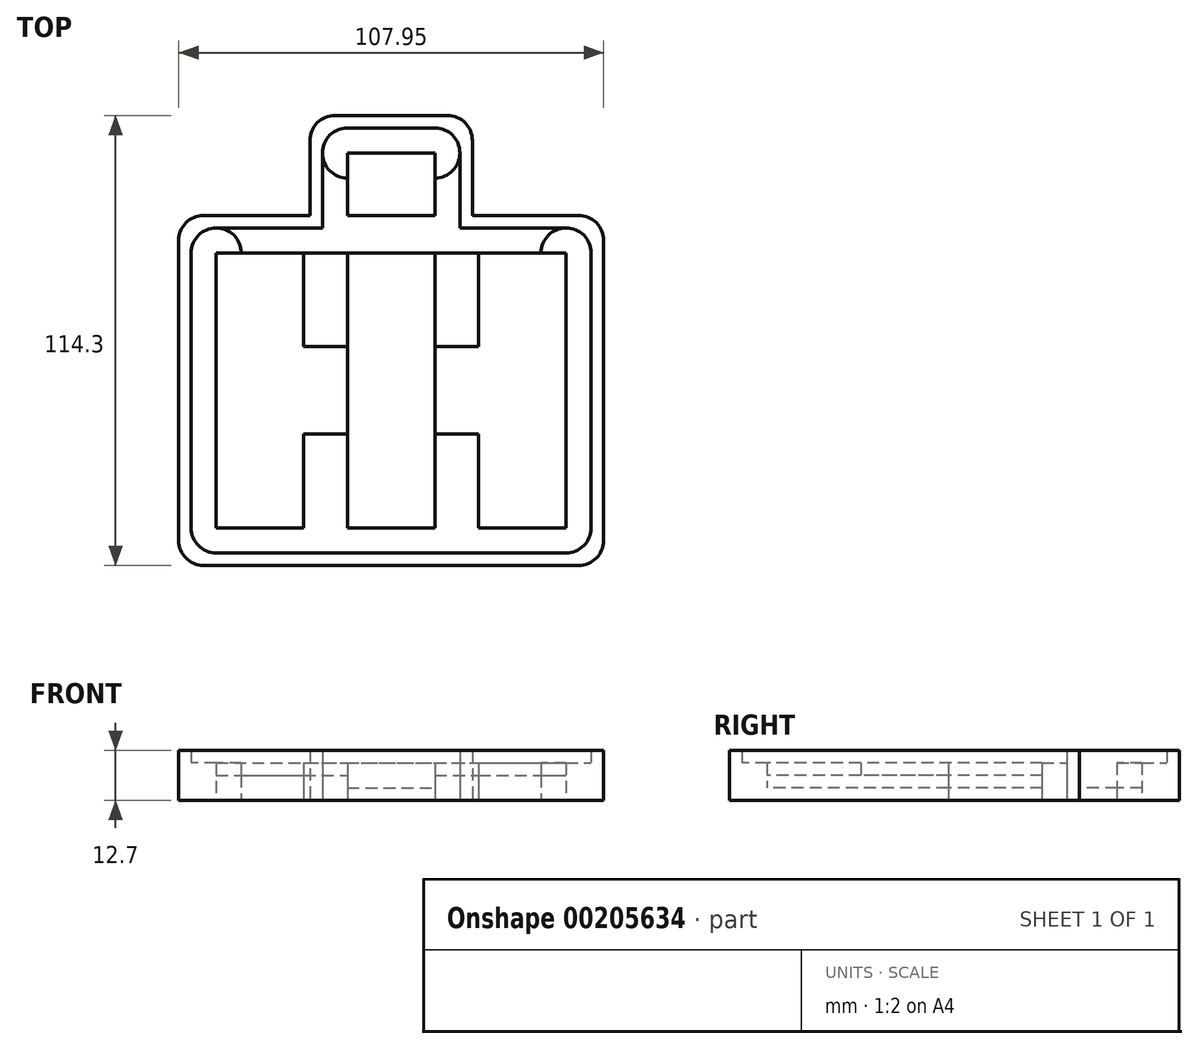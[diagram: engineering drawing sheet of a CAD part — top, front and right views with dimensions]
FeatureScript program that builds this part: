
annotation { "Feature Type Name" : "Feature", "Feature Type Description" : "" }
export const myFeature = defineFeature(function(context is Context, id is Id, definition is map)
    precondition{}
    {
        {
            var Q0;
            Q0=qCreatedBy(makeId("Top.planeOp"),FACE);
            var sketch = newSketch(context, id + "F0", { "sketchPlane" : qUnion([Q0])});
            skLineSegment(sketch, "E0.bottom", {"start": v(-34.36, 39.37) * mm, "end": v(-12.13, 39.37) * mm});
            skLineSegment(sketch, "E0.top", {"start": v(-34.36, -30.48) * mm, "end": v(-12.13, -30.48) * mm});
            skLineSegment(sketch, "E0.left", {"start": v(-34.36, 39.37) * mm, "end": v(-34.36, -30.48) * mm});
            skLineSegment(sketch, "E0.right", {"start": v(-12.13, 39.37) * mm, "end": v(-12.13, 15.56) * mm});
            skLineSegment(sketch, "E1.bottom", {"start": v(-12.13, 15.56) * mm, "end": v(32.32, 15.56) * mm});
            skLineSegment(sketch, "E1.top", {"start": v(-12.13, -6.67) * mm, "end": v(-1.02, -6.67) * mm});
            skLineSegment(sketch, "E1.left", {"start": v(-12.13, 15.56) * mm, "end": v(-12.13, -6.67) * mm});
            skLineSegment(sketch, "E1.right", {"start": v(32.32, 15.56) * mm, "end": v(32.32, 15.56) * mm});
            skLineSegment(sketch, "E2.bottom", {"start": v(32.32, 39.37) * mm, "end": v(54.54, 39.37) * mm});
            skLineSegment(sketch, "E2.top", {"start": v(32.32, -30.48) * mm, "end": v(54.54, -30.48) * mm});
            skLineSegment(sketch, "E2.left", {"start": v(32.32, 39.37) * mm, "end": v(32.32, 15.56) * mm});
            skLineSegment(sketch, "E2.right", {"start": v(54.54, 39.37) * mm, "end": v(54.54, -30.48) * mm});
            skLineSegment(sketch, "E3", {"start": v(-12.13, -6.67) * mm, "end": v(-12.13, -30.48) * mm});
            skLineSegment(sketch, "E4", {"start": v(32.32, 15.56) * mm, "end": v(32.32, -6.67) * mm});
            skLineSegment(sketch, "E5", {"start": v(32.32, -6.67) * mm, "end": v(32.32, -30.48) * mm});
            skLineSegment(sketch, "E6.bottom", {"start": v(-1.02, 39.37) * mm, "end": v(21.2, 39.37) * mm});
            skLineSegment(sketch, "E6.top", {"start": v(-1.02, -30.48) * mm, "end": v(21.2, -30.48) * mm});
            skLineSegment(sketch, "E6.left", {"start": v(-1.02, 39.37) * mm, "end": v(-1.02, -6.67) * mm});
            skLineSegment(sketch, "E6.right", {"start": v(21.2, 39.37) * mm, "end": v(21.2, 15.56) * mm});
            skLineSegment(sketch, "E7", {"start": v(21.2, 15.56) * mm, "end": v(21.2, -6.67) * mm});
            skLineSegment(sketch, "E8", {"start": v(21.2, -6.67) * mm, "end": v(21.2, -6.67) * mm});
            skLineSegment(sketch, "E9", {"start": v(-1.02, -6.67) * mm, "end": v(-1.02, -30.48) * mm});
            skLineSegment(sketch, "E10", {"start": v(21.2, -6.67) * mm, "end": v(21.2, -30.48) * mm});
            skLineSegment(sketch, "E11", {"start": v(21.2, -6.67) * mm, "end": v(32.32, -6.67) * mm});
            skLineSegment(sketch, "E12", {"start": v(-1.02, -6.67) * mm, "end": v(21.2, -6.67) * mm});
            skLineSegment(sketch, "E13.bottom", {"start": v(-1.02, 64.77) * mm, "end": v(21.2, 64.77) * mm});
            skLineSegment(sketch, "E13.top", {"start": v(-1.02, 45.72) * mm, "end": v(21.2, 45.72) * mm});
            skLineSegment(sketch, "E13.left", {"start": v(-1.02, 64.77) * mm, "end": v(-1.02, 45.72) * mm});
            skLineSegment(sketch, "E13.right", {"start": v(21.2, 64.77) * mm, "end": v(21.2, 45.72) * mm});
            skLineSegment(sketch, "E14.bottom", {"start": v(-34.36, 39.37) * mm, "end": v(54.54, 39.37) * mm});
            skLineSegment(sketch, "E14.top", {"start": v(-34.36, 45.72) * mm, "end": v(54.54, 45.72) * mm});
            skLineSegment(sketch, "E14.left", {"start": v(-34.36, 39.37) * mm, "end": v(-34.36, 45.72) * mm});
            skLineSegment(sketch, "E14.right", {"start": v(54.54, 39.37) * mm, "end": v(54.54, 45.72) * mm});
            skLineSegment(sketch, "E15.bottom", {"start": v(-34.36, -30.48) * mm, "end": v(54.54, -30.48) * mm});
            skLineSegment(sketch, "E15.top", {"start": v(-34.36, -36.83) * mm, "end": v(54.54, -36.83) * mm});
            skLineSegment(sketch, "E15.left", {"start": v(-34.36, -30.48) * mm, "end": v(-34.36, -36.83) * mm});
            skLineSegment(sketch, "E15.right", {"start": v(54.54, -30.48) * mm, "end": v(54.54, -36.83) * mm});
            skLineSegment(sketch, "E16.bottom", {"start": v(-34.36, 39.37) * mm, "end": v(-40.7, 39.37) * mm});
            skLineSegment(sketch, "E16.top", {"start": v(-34.36, -30.48) * mm, "end": v(-40.7, -30.48) * mm});
            skLineSegment(sketch, "E16.right", {"start": v(-40.7, 39.37) * mm, "end": v(-40.7, -30.48) * mm});
            skLineSegment(sketch, "E17.bottom", {"start": v(54.54, 39.37) * mm, "end": v(60.9, 39.37) * mm});
            skLineSegment(sketch, "E17.top", {"start": v(54.54, -30.48) * mm, "end": v(60.9, -30.48) * mm});
            skLineSegment(sketch, "E17.right", {"start": v(60.9, 39.37) * mm, "end": v(60.9, -30.48) * mm});
            skLineSegment(sketch, "E18.bottom", {"start": v(21.2, 64.77) * mm, "end": v(27.55, 64.77) * mm});
            skLineSegment(sketch, "E18.top", {"start": v(21.2, 45.72) * mm, "end": v(27.55, 45.72) * mm});
            skLineSegment(sketch, "E18.right", {"start": v(27.55, 64.77) * mm, "end": v(27.55, 45.72) * mm});
            skLineSegment(sketch, "E19.bottom", {"start": v(-1.02, 64.77) * mm, "end": v(-7.37, 64.77) * mm});
            skLineSegment(sketch, "E19.top", {"start": v(-1.02, 45.72) * mm, "end": v(-7.37, 45.72) * mm});
            skLineSegment(sketch, "E19.right", {"start": v(-7.37, 64.77) * mm, "end": v(-7.37, 45.72) * mm});
            skLineSegment(sketch, "E20.top", {"start": v(-1.02, 71.12) * mm, "end": v(21.2, 71.12) * mm});
            skLineSegment(sketch, "E20.left", {"start": v(-1.02, 64.77) * mm, "end": v(-1.02, 71.12) * mm});
            skLineSegment(sketch, "E20.right", {"start": v(21.2, 64.77) * mm, "end": v(21.2, 71.12) * mm});
            skCircle(sketch, "E21", {"center": v(-34.36, 39.37) * mm, "radius": 6.35 * mm});
            skCircle(sketch, "E22", {"center": v(54.54, 39.37) * mm, "radius": 6.35 * mm});
            skCircle(sketch, "E23", {"center": v(-34.36, -30.48) * mm, "radius": 6.35 * mm});
            skCircle(sketch, "E24", {"center": v(54.54, -30.48) * mm, "radius": 6.35 * mm});
            skCircle(sketch, "E25", {"center": v(21.2, 64.77) * mm, "radius": 6.35 * mm});
            skCircle(sketch, "E26", {"center": v(-1.02, 64.77) * mm, "radius": 6.35 * mm});
            skLineSegment(sketch, "E27.bottom", {"start": v(-43.88, 48.9) * mm, "end": v(64.07, 48.9) * mm});
            skLineSegment(sketch, "E27.top", {"start": v(-43.88, -40) * mm, "end": v(64.07, -40) * mm});
            skLineSegment(sketch, "E27.left", {"start": v(-43.88, 48.9) * mm, "end": v(-43.88, -40) * mm});
            skLineSegment(sketch, "E27.right", {"start": v(64.07, 48.9) * mm, "end": v(64.07, -40) * mm});
            skLineSegment(sketch, "E28.bottom", {"start": v(-10.55, 48.9) * mm, "end": v(30.73, 48.9) * mm});
            skLineSegment(sketch, "E28.top", {"start": v(-10.55, 74.3) * mm, "end": v(30.73, 74.3) * mm});
            skLineSegment(sketch, "E28.left", {"start": v(-10.55, 48.9) * mm, "end": v(-10.55, 74.3) * mm});
            skLineSegment(sketch, "E28.right", {"start": v(30.73, 48.9) * mm, "end": v(30.73, 74.3) * mm});
            skSolve(sketch);
        }
        {
            var Q0;
            {var subQ0=sQuery(id+"F0.wireOp",EDGE,"E6.right");Q0=makeQuery(id+"F0.imprint","IMPRINT",FACE,{"disambiguationData":[TD([[makeQuery(id+"F0.imprint","IMPRINT",EDGE,{"derivedFrom":subQ0}),-1.0]])]});}
            var Q1;
            {var subQ0=sQuery(id+"F0.wireOp",EDGE,"E7");Q1=makeQuery(id+"F0.imprint","IMPRINT",FACE,{"disambiguationData":[TD([[makeQuery(id+"F0.imprint","IMPRINT",EDGE,{"derivedFrom":subQ0}),-1.0]])]});}
            var Q2;
            {var subQ0=sQuery(id+"F0.wireOp",EDGE,"E9");Q2=makeQuery(id+"F0.imprint","IMPRINT",FACE,{"disambiguationData":[TD([[makeQuery(id+"F0.imprint","IMPRINT",EDGE,{"derivedFrom":subQ0}),1.0]])]});}
            var Q3;
            {var subQ0=sQuery(id+"F0.wireOp",EDGE,"E26");var subQ1=sQuery(id+"F0.wireOp",EDGE,"E13.bottom");var subQ2=makeQuery(id+"F0.imprint","INTERSECT",VERTEX,{"derivedFrom":[subQ1,subQ0]});Q3=makeQuery(id+"F0.imprint","IMPRINT",FACE,{"disambiguationData":[TD([[makeQuery(id+"F0.imprint","IMPRINT",EDGE,{"disambiguationData":[TD([[subQ2,-1.0]])],"derivedFrom":subQ1}),-1.0]])]});}
            var Q4;
            {var subQ1=sQuery(id+"F0.wireOp",EDGE,"E13.left");var subQ3=sQuery(id+"F0.wireOp",EDGE,"E26");var subQ4=makeQuery(id+"F0.imprint","INTERSECT",VERTEX,{"derivedFrom":[subQ1,subQ3]});Q4=makeQuery(id+"F0.imprint","IMPRINT",FACE,{"disambiguationData":[TD([[makeQuery(id+"F0.imprint","IMPRINT",EDGE,{"disambiguationData":[TD([[subQ4,-1.0]])],"derivedFrom":subQ3}),1.0]])]});}
            var Q5;
            {var subQ1=sQuery(id+"F0.wireOp",EDGE,"E13.right");var subQ3=sQuery(id+"F0.wireOp",EDGE,"E25");var subQ4=makeQuery(id+"F0.imprint","INTERSECT",VERTEX,{"derivedFrom":[subQ1,subQ3]});Q5=makeQuery(id+"F0.imprint","IMPRINT",FACE,{"disambiguationData":[TD([[makeQuery(id+"F0.imprint","IMPRINT",EDGE,{"disambiguationData":[TD([[subQ4,1.0]])],"derivedFrom":subQ3}),1.0]])]});}
            extrude(context, id + "F1", {"entities" : qUnion([Q0, Q1, Q2, Q3, Q4, Q5]), "depth" : 3.17 * mm});
        }
        {
            var Q0;
            {var subQ1=sQuery(id+"F0.wireOp",EDGE,"E2.left");Q0=makeQuery(id+"F0.imprint","IMPRINT",FACE,{"disambiguationData":[TD([[makeQuery(id+"F0.imprint","IMPRINT",EDGE,{"derivedFrom":subQ1}),1.0]])]});}
            var Q1;
            {var subQ1=sQuery(id+"F0.wireOp",EDGE,"E0.right");Q1=makeQuery(id+"F0.imprint","IMPRINT",FACE,{"disambiguationData":[TD([[makeQuery(id+"F0.imprint","IMPRINT",EDGE,{"derivedFrom":subQ1}),-1.0]])]});}
            var Q2;
            {var subQ4=sQuery(id+"F0.wireOp",EDGE,"E1.top");Q2=makeQuery(id+"F0.imprint","IMPRINT",FACE,{"disambiguationData":[TD([[makeQuery(id+"F0.imprint","IMPRINT",EDGE,{"derivedFrom":subQ4}),1.0]])]});}
            var Q3;
            {var subQ0=sQuery(id+"F0.wireOp",EDGE,"E4");Q3=makeQuery(id+"F0.imprint","IMPRINT",FACE,{"disambiguationData":[TD([[makeQuery(id+"F0.imprint","IMPRINT",EDGE,{"derivedFrom":subQ0}),-1.0]])]});}
            var Q4;
            {var subQ1=sQuery(id+"F0.wireOp",EDGE,"E14.bottom");var subQ3=sQuery(id+"F0.wireOp",EDGE,"E21");var subQ4=makeQuery(id+"F0.imprint","INTERSECT",VERTEX,{"derivedFrom":[subQ1,subQ3]});Q4=makeQuery(id+"F0.imprint","IMPRINT",FACE,{"disambiguationData":[TD([[makeQuery(id+"F0.imprint","IMPRINT",EDGE,{"disambiguationData":[TD([[subQ4,1.0]])],"derivedFrom":subQ3}),1.0]])]});}
            var Q5;
            {var subQ1=sQuery(id+"F0.wireOp",EDGE,"E15.bottom");var subQ3=sQuery(id+"F0.wireOp",EDGE,"E23");var subQ4=makeQuery(id+"F0.imprint","INTERSECT",VERTEX,{"derivedFrom":[subQ1,subQ3]});Q5=makeQuery(id+"F0.imprint","IMPRINT",FACE,{"disambiguationData":[TD([[makeQuery(id+"F0.imprint","IMPRINT",EDGE,{"disambiguationData":[TD([[subQ4,-1.0]])],"derivedFrom":subQ3}),1.0]])]});}
            var Q6;
            {var subQ1=sQuery(id+"F0.wireOp",EDGE,"E14.bottom");var subQ3=sQuery(id+"F0.wireOp",EDGE,"E22");var subQ4=makeQuery(id+"F0.imprint","INTERSECT",VERTEX,{"derivedFrom":[subQ1,subQ3]});Q6=makeQuery(id+"F0.imprint","IMPRINT",FACE,{"disambiguationData":[TD([[makeQuery(id+"F0.imprint","IMPRINT",EDGE,{"disambiguationData":[TD([[subQ4,-1.0]])],"derivedFrom":subQ3}),1.0]])]});}
            var Q7;
            {var subQ1=sQuery(id+"F0.wireOp",EDGE,"E15.bottom");var subQ3=sQuery(id+"F0.wireOp",EDGE,"E24");var subQ4=makeQuery(id+"F0.imprint","INTERSECT",VERTEX,{"derivedFrom":[subQ1,subQ3]});Q7=makeQuery(id+"F0.imprint","IMPRINT",FACE,{"disambiguationData":[TD([[makeQuery(id+"F0.imprint","IMPRINT",EDGE,{"disambiguationData":[TD([[subQ4,1.0]])],"derivedFrom":subQ3}),1.0]])]});}
            extrude(context, id + "F2", {"entities" : qUnion([Q0, Q1, Q2, Q3, Q4, Q5, Q6, Q7]), "operationType" : NewBodyOperationType.ADD, "depth" : 6.35 * mm});
        }
        {
            var Q0;
            {var subQ0=sQuery(id+"F0.wireOp",EDGE,"E14.left");Q0=makeQuery(id+"F0.imprint","IMPRINT",FACE,{"disambiguationData":[TD([[makeQuery(id+"F0.imprint","IMPRINT",EDGE,{"derivedFrom":subQ0}),1.0]])]});}
            var Q1;
            {var subQ0=sQuery(id+"F0.wireOp",EDGE,"E14.left");Q1=makeQuery(id+"F0.imprint","IMPRINT",FACE,{"disambiguationData":[TD([[makeQuery(id+"F0.imprint","IMPRINT",EDGE,{"derivedFrom":subQ0}),-1.0]])]});}
            var Q2;
            {var subQ0=sQuery(id+"F0.wireOp",EDGE,"E18.top");Q2=makeQuery(id+"F0.imprint","IMPRINT",FACE,{"disambiguationData":[TD([[makeQuery(id+"F0.imprint","IMPRINT",EDGE,{"derivedFrom":subQ0}),-1.0]])]});}
            var Q3;
            {var subQ0=sQuery(id+"F0.wireOp",EDGE,"E14.right");Q3=makeQuery(id+"F0.imprint","IMPRINT",FACE,{"disambiguationData":[TD([[makeQuery(id+"F0.imprint","IMPRINT",EDGE,{"derivedFrom":subQ0}),1.0]])]});}
            var Q4;
            {var subQ0=sQuery(id+"F0.wireOp",EDGE,"E14.right");Q4=makeQuery(id+"F0.imprint","IMPRINT",FACE,{"disambiguationData":[TD([[makeQuery(id+"F0.imprint","IMPRINT",EDGE,{"derivedFrom":subQ0}),-1.0]])]});}
            var Q5;
            {var subQ0=sQuery(id+"F0.wireOp",EDGE,"E17.bottom");Q5=makeQuery(id+"F0.imprint","IMPRINT",FACE,{"disambiguationData":[TD([[makeQuery(id+"F0.imprint","IMPRINT",EDGE,{"derivedFrom":subQ0}),-1.0]])]});}
            var Q6;
            {var subQ5=sQuery(id+"F0.wireOp",EDGE,"E17.right");Q6=makeQuery(id+"F0.imprint","IMPRINT",FACE,{"disambiguationData":[TD([[makeQuery(id+"F0.imprint","IMPRINT",EDGE,{"derivedFrom":subQ5}),-1.0]])]});}
            var Q7;
            {var subQ0=sQuery(id+"F0.wireOp",EDGE,"E17.top");Q7=makeQuery(id+"F0.imprint","IMPRINT",FACE,{"disambiguationData":[TD([[makeQuery(id+"F0.imprint","IMPRINT",EDGE,{"derivedFrom":subQ0}),1.0]])]});}
            var Q8;
            {var subQ0=sQuery(id+"F0.wireOp",EDGE,"E15.right");Q8=makeQuery(id+"F0.imprint","IMPRINT",FACE,{"disambiguationData":[TD([[makeQuery(id+"F0.imprint","IMPRINT",EDGE,{"derivedFrom":subQ0}),1.0]])]});}
            var Q9;
            {var subQ0=sQuery(id+"F0.wireOp",EDGE,"E15.right");Q9=makeQuery(id+"F0.imprint","IMPRINT",FACE,{"disambiguationData":[TD([[makeQuery(id+"F0.imprint","IMPRINT",EDGE,{"derivedFrom":subQ0}),-1.0]])]});}
            var Q10;
            {var subQ7=sQuery(id+"F0.wireOp",EDGE,"E15.top");Q10=makeQuery(id+"F0.imprint","IMPRINT",FACE,{"disambiguationData":[TD([[makeQuery(id+"F0.imprint","IMPRINT",EDGE,{"derivedFrom":subQ7}),1.0]])]});}
            var Q11;
            {var subQ0=sQuery(id+"F0.wireOp",EDGE,"E15.left");Q11=makeQuery(id+"F0.imprint","IMPRINT",FACE,{"disambiguationData":[TD([[makeQuery(id+"F0.imprint","IMPRINT",EDGE,{"derivedFrom":subQ0}),1.0]])]});}
            var Q12;
            {var subQ0=sQuery(id+"F0.wireOp",EDGE,"E15.left");Q12=makeQuery(id+"F0.imprint","IMPRINT",FACE,{"disambiguationData":[TD([[makeQuery(id+"F0.imprint","IMPRINT",EDGE,{"derivedFrom":subQ0}),-1.0]])]});}
            var Q13;
            {var subQ5=sQuery(id+"F0.wireOp",EDGE,"E16.right");Q13=makeQuery(id+"F0.imprint","IMPRINT",FACE,{"disambiguationData":[TD([[makeQuery(id+"F0.imprint","IMPRINT",EDGE,{"derivedFrom":subQ5}),1.0]])]});}
            var Q14;
            {var subQ0=sQuery(id+"F0.wireOp",EDGE,"E16.top");Q14=makeQuery(id+"F0.imprint","IMPRINT",FACE,{"disambiguationData":[TD([[makeQuery(id+"F0.imprint","IMPRINT",EDGE,{"derivedFrom":subQ0}),-1.0]])]});}
            var Q15;
            {var subQ0=sQuery(id+"F0.wireOp",EDGE,"E16.bottom");Q15=makeQuery(id+"F0.imprint","IMPRINT",FACE,{"disambiguationData":[TD([[makeQuery(id+"F0.imprint","IMPRINT",EDGE,{"derivedFrom":subQ0}),1.0]])]});}
            var Q16;
            {var subQ0=sQuery(id+"F0.wireOp",EDGE,"E0.right");Q16=makeQuery(id+"F0.imprint","IMPRINT",FACE,{"disambiguationData":[TD([[makeQuery(id+"F0.imprint","IMPRINT",EDGE,{"derivedFrom":subQ0}),1.0]])]});}
            var Q17;
            {var subQ0=sQuery(id+"F0.wireOp",EDGE,"E2.left");Q17=makeQuery(id+"F0.imprint","IMPRINT",FACE,{"disambiguationData":[TD([[makeQuery(id+"F0.imprint","IMPRINT",EDGE,{"derivedFrom":subQ0}),-1.0]])]});}
            var Q18;
            Q18=makeQuery(id+"F0.imprint","IMPRINT",FACE,{"disambiguationData":[TD([[makeQuery(id+"F0.imprint","IMPRINT",EDGE,{"derivedFrom":sQuery(id+"F0.wireOp",EDGE,"E1.top")}),-1.0]])]});
            var Q19;
            {var subQ0=sQuery(id+"F0.wireOp",EDGE,"E5");Q19=makeQuery(id+"F0.imprint","IMPRINT",FACE,{"disambiguationData":[TD([[makeQuery(id+"F0.imprint","IMPRINT",EDGE,{"derivedFrom":subQ0}),-1.0]])]});}
            var Q20;
            {var subQ0=sQuery(id+"F0.wireOp",EDGE,"E19.top");Q20=makeQuery(id+"F0.imprint","IMPRINT",FACE,{"disambiguationData":[TD([[makeQuery(id+"F0.imprint","IMPRINT",EDGE,{"derivedFrom":subQ0}),-1.0]])]});}
            var Q21;
            {var subQ0=sQuery(id+"F0.wireOp",EDGE,"E13.right");var subQ5=sQuery(id+"F0.wireOp",EDGE,"E28.bottom");var subQ6=makeQuery(id+"F0.imprint","INTERSECT",VERTEX,{"derivedFrom":[subQ0,subQ5]});Q21=makeQuery(id+"F0.imprint","IMPRINT",FACE,{"disambiguationData":[TD([[makeQuery(id+"F0.imprint","IMPRINT",EDGE,{"disambiguationData":[TD([[subQ6,1.0]])],"derivedFrom":subQ5}),-1.0]])]});}
            var Q22;
            {var subQ0=sQuery(id+"F0.wireOp",EDGE,"E18.top");Q22=makeQuery(id+"F0.imprint","IMPRINT",FACE,{"disambiguationData":[TD([[makeQuery(id+"F0.imprint","IMPRINT",EDGE,{"derivedFrom":subQ0}),1.0]])]});}
            var Q23;
            {var subQ0=sQuery(id+"F0.wireOp",EDGE,"E25");var subQ1=sQuery(id+"F0.wireOp",EDGE,"E13.right");var subQ2=makeQuery(id+"F0.imprint","INTERSECT",VERTEX,{"derivedFrom":[subQ1,subQ0]});Q23=makeQuery(id+"F0.imprint","IMPRINT",FACE,{"disambiguationData":[TD([[makeQuery(id+"F0.imprint","IMPRINT",EDGE,{"disambiguationData":[TD([[subQ2,-1.0]])],"derivedFrom":subQ1}),1.0]])]});}
            var Q24;
            {var subQ0=sQuery(id+"F0.wireOp",EDGE,"E18.bottom");Q24=makeQuery(id+"F0.imprint","IMPRINT",FACE,{"disambiguationData":[TD([[makeQuery(id+"F0.imprint","IMPRINT",EDGE,{"derivedFrom":subQ0}),-1.0]])]});}
            var Q25;
            {var subQ0=sQuery(id+"F0.wireOp",EDGE,"E18.bottom");Q25=makeQuery(id+"F0.imprint","IMPRINT",FACE,{"disambiguationData":[TD([[makeQuery(id+"F0.imprint","IMPRINT",EDGE,{"derivedFrom":subQ0}),1.0]])]});}
            var Q26;
            {var subQ0=sQuery(id+"F0.wireOp",EDGE,"E20.right");Q26=makeQuery(id+"F0.imprint","IMPRINT",FACE,{"disambiguationData":[TD([[makeQuery(id+"F0.imprint","IMPRINT",EDGE,{"derivedFrom":subQ0}),1.0]])]});}
            var Q27;
            {var subQ5=sQuery(id+"F0.wireOp",EDGE,"E20.top");Q27=makeQuery(id+"F0.imprint","IMPRINT",FACE,{"disambiguationData":[TD([[makeQuery(id+"F0.imprint","IMPRINT",EDGE,{"derivedFrom":subQ5}),-1.0]])]});}
            var Q28;
            {var subQ0=sQuery(id+"F0.wireOp",EDGE,"E20.left");Q28=makeQuery(id+"F0.imprint","IMPRINT",FACE,{"disambiguationData":[TD([[makeQuery(id+"F0.imprint","IMPRINT",EDGE,{"derivedFrom":subQ0}),-1.0]])]});}
            var Q29;
            {var subQ0=sQuery(id+"F0.wireOp",EDGE,"E19.bottom");Q29=makeQuery(id+"F0.imprint","IMPRINT",FACE,{"disambiguationData":[TD([[makeQuery(id+"F0.imprint","IMPRINT",EDGE,{"derivedFrom":subQ0}),-1.0]])]});}
            var Q30;
            {var subQ0=sQuery(id+"F0.wireOp",EDGE,"E19.bottom");Q30=makeQuery(id+"F0.imprint","IMPRINT",FACE,{"disambiguationData":[TD([[makeQuery(id+"F0.imprint","IMPRINT",EDGE,{"derivedFrom":subQ0}),1.0]])]});}
            var Q31;
            {var subQ0=sQuery(id+"F0.wireOp",EDGE,"E26");var subQ1=sQuery(id+"F0.wireOp",EDGE,"E13.left");var subQ2=makeQuery(id+"F0.imprint","INTERSECT",VERTEX,{"derivedFrom":[subQ1,subQ0]});Q31=makeQuery(id+"F0.imprint","IMPRINT",FACE,{"disambiguationData":[TD([[makeQuery(id+"F0.imprint","IMPRINT",EDGE,{"disambiguationData":[TD([[subQ2,-1.0]])],"derivedFrom":subQ1}),-1.0]])]});}
            extrude(context, id + "F3", {"entities" : qUnion([Q0, Q1, Q2, Q3, Q4, Q5, Q6, Q7, Q8, Q9, Q10, Q11, Q12, Q13, Q14, Q15, Q16, Q17, Q18, Q19, Q20, Q21, Q22, Q23, Q24, Q25, Q26, Q27, Q28, Q29, Q30, Q31]), "depth" : 9.52 * mm});
        }
        {
            var Q0;
            {var subQ13=sQuery(id+"F0.wireOp",EDGE,"E15.top");Q0=makeQuery(id+"F0.imprint","IMPRINT",FACE,{"disambiguationData":[TD([[makeQuery(id+"F0.imprint","IMPRINT",EDGE,{"derivedFrom":subQ13}),-1.0]])]});}
            var Q1;
            {var subQ0=sQuery(id+"F0.wireOp",EDGE,"E20.top");Q1=makeQuery(id+"F0.imprint","IMPRINT",FACE,{"disambiguationData":[TD([[makeQuery(id+"F0.imprint","IMPRINT",EDGE,{"derivedFrom":subQ0}),1.0]])]});}
            extrude(context, id + "F4", {"entities" : qUnion([Q0, Q1]), "operationType" : NewBodyOperationType.ADD, "depth" : 12.7 * mm});
        }
        {
            var Q0;
            Q0=makeQuery(id+"F4.opExtrude","SWEPT_EDGE",EDGE,{"disambiguationData":[OSD([sQuery(id+"F0.wireOp",EDGE,"E27.bottom"),sQuery(id+"F0.wireOp",EDGE,"E27.left")])]});
            var Q1;
            Q1=makeQuery(id+"F4.opExtrude","SWEPT_EDGE",EDGE,{"disambiguationData":[OSD([sQuery(id+"F0.wireOp",EDGE,"E27.bottom"),sQuery(id+"F0.wireOp",EDGE,"E27.right")])]});
            var Q2;
            Q2=makeQuery(id+"F4.opExtrude","SWEPT_EDGE",EDGE,{"disambiguationData":[OSD([sQuery(id+"F0.wireOp",EDGE,"E27.top"),sQuery(id+"F0.wireOp",EDGE,"E27.right")])]});
            var Q3;
            Q3=makeQuery(id+"F4.opExtrude","SWEPT_EDGE",EDGE,{"disambiguationData":[OSD([sQuery(id+"F0.wireOp",EDGE,"E27.top"),sQuery(id+"F0.wireOp",EDGE,"E27.left")])]});
            var Q4;
            Q4=makeQuery(id+"F4.opExtrude","SWEPT_EDGE",EDGE,{"disambiguationData":[OSD([sQuery(id+"F0.wireOp",EDGE,"E28.top"),sQuery(id+"F0.wireOp",EDGE,"E28.left")])]});
            var Q5;
            Q5=makeQuery(id+"F4.opExtrude","SWEPT_EDGE",EDGE,{"disambiguationData":[OSD([sQuery(id+"F0.wireOp",EDGE,"E28.top"),sQuery(id+"F0.wireOp",EDGE,"E28.right")])]});
            fillet(context, id + "F5", {"entities" : qUnion([Q0, Q1, Q2, Q3, Q4, Q5]), "radius" : 6.35 * mm, "tangentPropagation" : true, "allowEdgeOverflow" : false});
        }
    });
